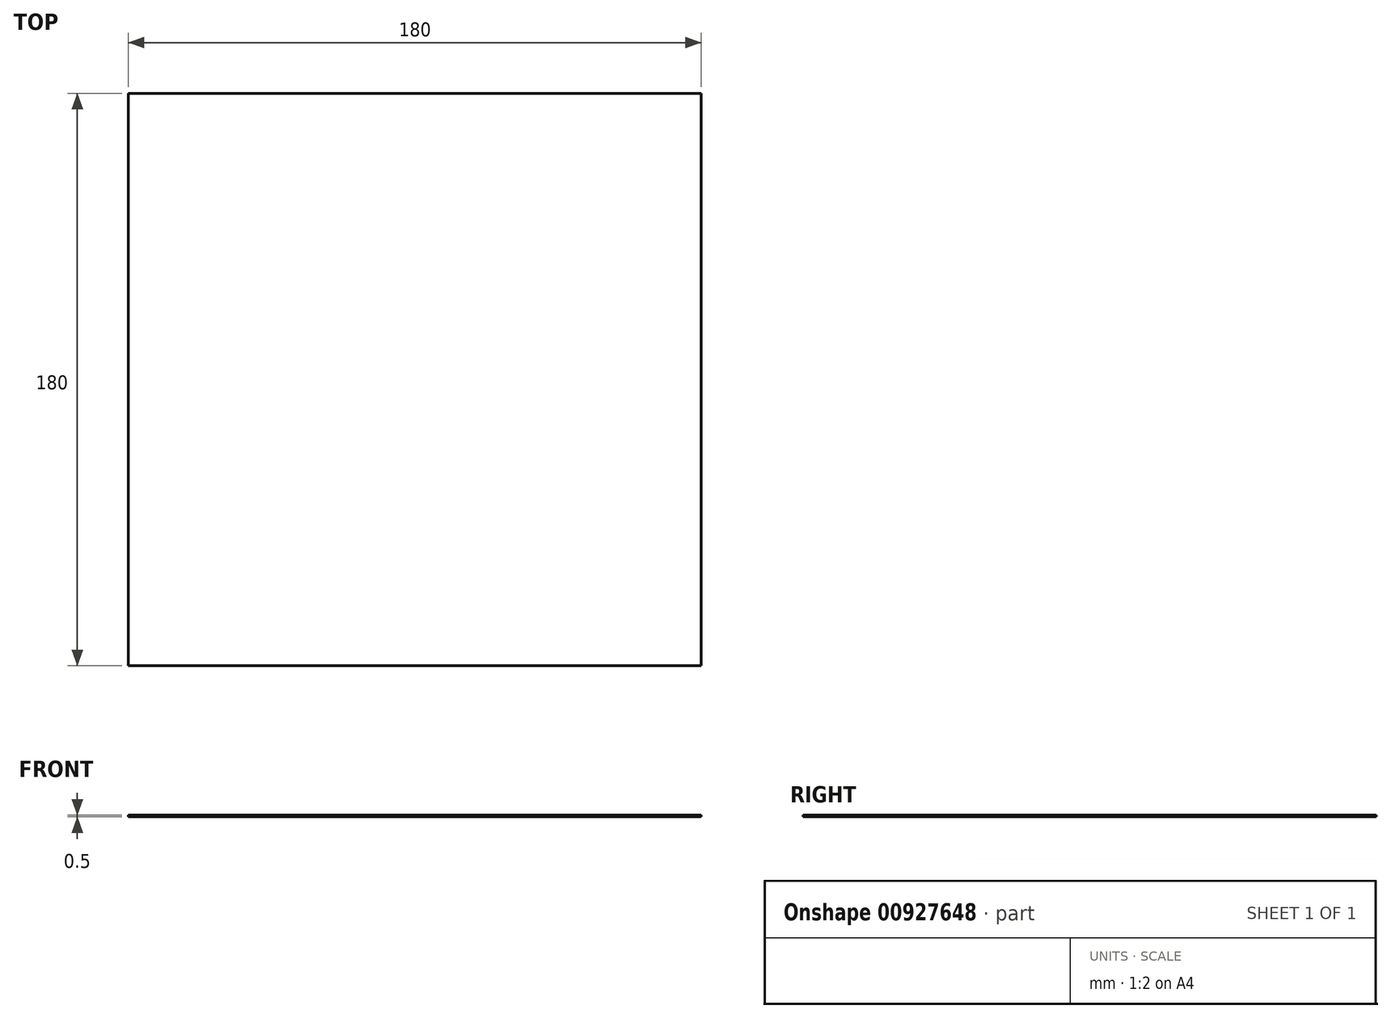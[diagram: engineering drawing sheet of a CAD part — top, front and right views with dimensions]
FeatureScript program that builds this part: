
annotation { "Feature Type Name" : "Feature", "Feature Type Description" : "" }
export const myFeature = defineFeature(function(context is Context, id is Id, definition is map)
    precondition{}
    {
        {
            var Q0;
            Q0=qCreatedBy(makeId("Top.planeOp"),FACE);
            var sketch = newSketch(context, id + "F0", { "sketchPlane" : qUnion([Q0])});
            skLineSegment(sketch, "E0.bottom", {"start": v(90, -90) * mm, "end": v(-90, -90) * mm});
            skLineSegment(sketch, "E0.top", {"start": v(90, 90) * mm, "end": v(-90, 90) * mm});
            skLineSegment(sketch, "E0.left", {"start": v(90, -90) * mm, "end": v(90, 90) * mm});
            skLineSegment(sketch, "E0.right", {"start": v(-90, -90) * mm, "end": v(-90, 90) * mm});
            skPoint(sketch, "E0.middle", {"position": v(0, 0) * mm});
            skSolve(sketch);
        }
        {
            var Q0;
            Q0 = qSketchRegion(id + "F0", true);
            extrude(context, id + "F1", {"entities" : qUnion([Q0]), "depth" : 0.5 * mm, "offsetDistance" : 25 * mm});
        }
    });
